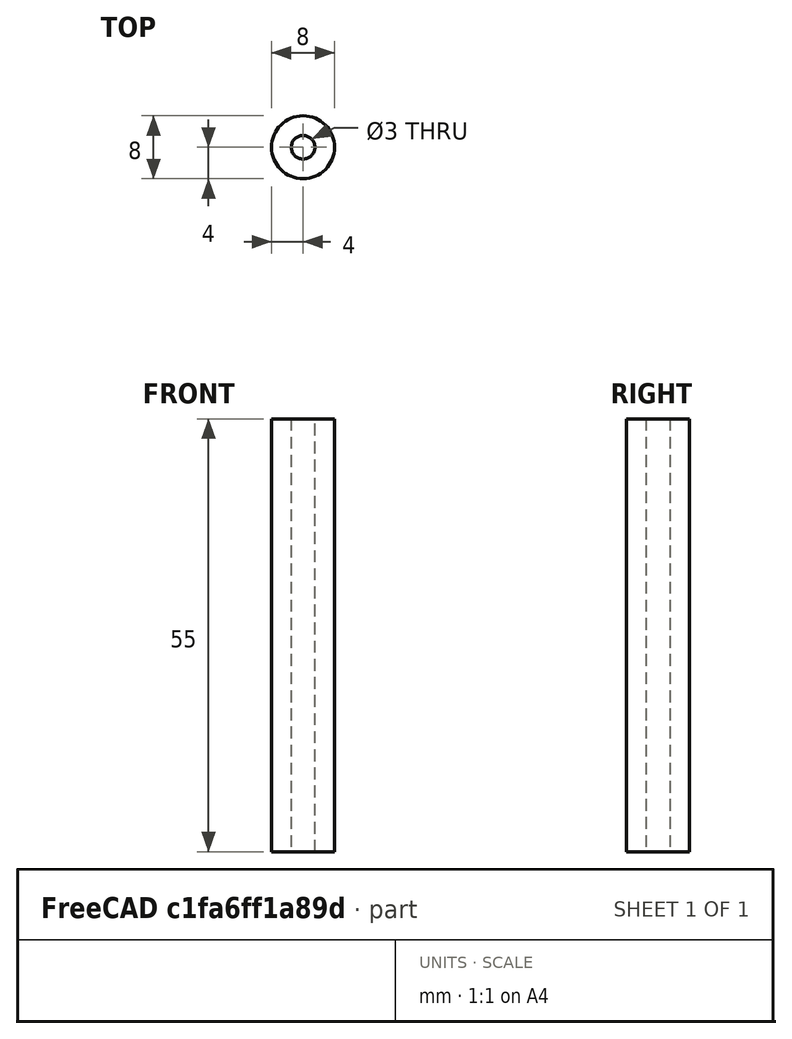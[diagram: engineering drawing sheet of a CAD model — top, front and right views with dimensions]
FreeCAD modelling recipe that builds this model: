
FCSTD DOCUMENT  (FreeCAD 1.0R39109 (Git))
Label: barrelSpacer
License: All rights reserved
LicenseURL: https://en.wikipedia.org/wiki/All_rights_reserved
objects: Sketcher::SketchObject×1, PartDesign::Pad×1, PartDesign::Body×1
note: 6 computed .brp shape members not serialized (recipe doc carries the construction recipe); baked Part::Feature solids carry a one-line shape summary decoded from their .brp

FEATURE [Sketcher::SketchObject] Sketch
  ArcFitTolerance = 1e-06
  AttachmentSupport = -> [XY_Plane]
  FullyConstrained = true
  MakeInternals = false
  MapMode = 5
  sketch-geometry (2):
    g0: Circle CenterX=0 CenterY=0 CenterZ=0 NormalX=0 NormalY=0 NormalZ=1 AngleXU=0 Radius=1.5
    g1: Circle CenterX=0 CenterY=0 CenterZ=0 NormalX=0 NormalY=0 NormalZ=1 AngleXU=0 Radius=4
  constraints (4):
    c: Coincident(g0,g-1)
    c: Coincident(g1,g0)
    c: Diameter(g0) = 3
    c: Distance(g0,g1) = 2.5
FEATURE [PartDesign::Pad] Pad
  Direction = (0,0,1)
  Length = 55
  Length2 = 10
  Profile = -> Sketch
  ReferenceAxis = -> Sketch [N_Axis]
  Refine = true
  Suppressed = false
  Type = 0
FEATURE [PartDesign::Body] Body
  AllowCompound = false
  Group = -> [Sketch,Pad]
  Origin = -> Origin
  Tip = -> Pad
